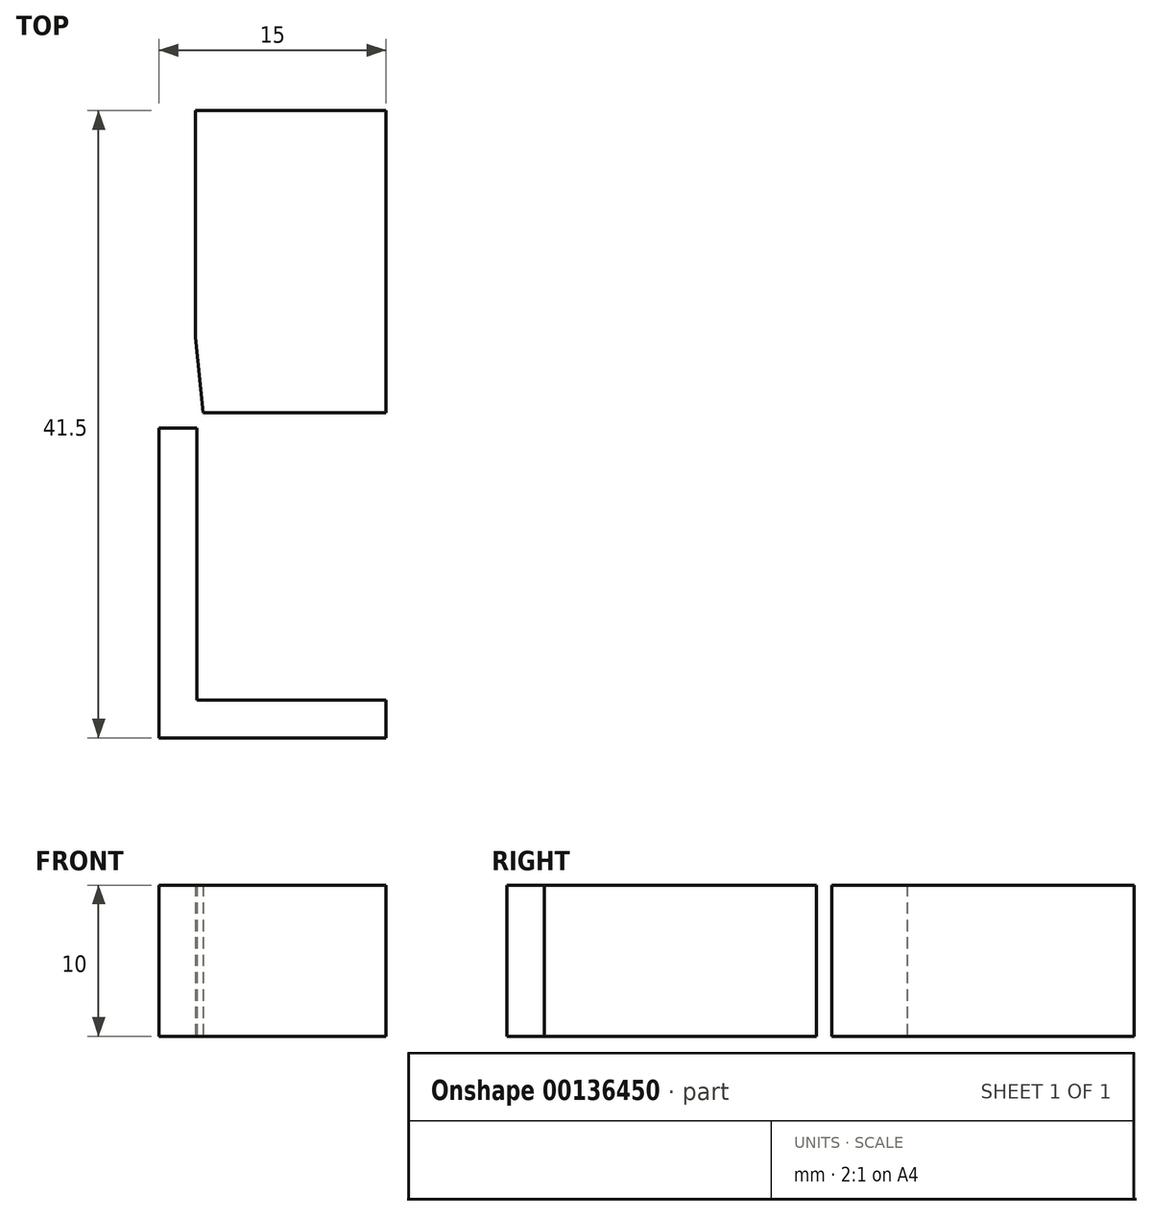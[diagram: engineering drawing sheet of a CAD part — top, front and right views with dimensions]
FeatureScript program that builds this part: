
annotation { "Feature Type Name" : "Feature", "Feature Type Description" : "" }
export const myFeature = defineFeature(function(context is Context, id is Id, definition is map)
    precondition{}
    {
        {
            var Q0;
            Q0=qCreatedBy(makeId("Top.planeOp"),FACE);
            var sketch = newSketch(context, id + "F0", { "sketchPlane" : qUnion([Q0])});
            skLineSegment(sketch, "E0.bottom", {"start": v(0, 0) * mm, "end": v(-2.5, 0) * mm});
            skLineSegment(sketch, "E0.left", {"start": v(0, 0) * mm, "end": v(0, -18) * mm});
            skLineSegment(sketch, "E0.right", {"start": v(-2.5, 0) * mm, "end": v(-2.5, -18) * mm});
            skLineSegment(sketch, "E1.bottom", {"start": v(0, -18) * mm, "end": v(12.5, -18) * mm});
            skLineSegment(sketch, "E1.top", {"start": v(-2.5, -20.5) * mm, "end": v(12.5, -20.5) * mm});
            skLineSegment(sketch, "E1.left", {"start": v(-2.5, -18) * mm, "end": v(-2.5, -20.5) * mm});
            skLineSegment(sketch, "E1.right", {"start": v(12.5, -18) * mm, "end": v(12.5, -20.5) * mm});
            skLineSegment(sketch, "E2", {"start": v(12.5, 1) * mm, "end": v(12.5, 12.95) * mm, "construction": true});
            skLineSegment(sketch, "E3.bottom", {"start": v(12.5, 1) * mm, "end": v(0.4, 1) * mm});
            skLineSegment(sketch, "E3.top", {"start": v(12.5, 21) * mm, "end": v(-0.1, 21) * mm});
            skLineSegment(sketch, "E3.left", {"start": v(12.5, 1) * mm, "end": v(12.5, 21) * mm});
            skLineSegment(sketch, "E3.right", {"start": v(-0.1, 6) * mm, "end": v(-0.1, 21) * mm});
            skPoint(sketch, "E4", {"position": v(0.4, 1) * mm});
            skLineSegment(sketch, "E5", {"start": v(0.4, 1) * mm, "end": v(-0.1, 6) * mm});
            skPoint(sketch, "E6.orphan", {"position": v(-0.1, 1) * mm});
            skSolve(sketch);
        }
        {
            var Q0;
            Q0=makeQuery(id+"F0.imprint","IMPRINT",FACE,{"disambiguationData":[TD([[makeQuery(id+"F0.imprint","IMPRINT",EDGE,{"derivedFrom":sQuery(id+"F0.wireOp",EDGE,"E3.bottom")}),-1.0]])]});
            var Q1;
            Q1=makeQuery(id+"F0.imprint","IMPRINT",FACE,{"disambiguationData":[TD([[makeQuery(id+"F0.imprint","IMPRINT",EDGE,{"derivedFrom":sQuery(id+"F0.wireOp",EDGE,"E0.bottom")}),1.0]])]});
            extrude(context, id + "F1", {"entities" : qUnion([Q0, Q1]), "depth" : 10 * mm});
        }
    });
